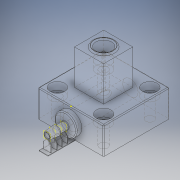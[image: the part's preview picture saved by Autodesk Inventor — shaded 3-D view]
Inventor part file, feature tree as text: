
AUTODESK INVENTOR PART (.ipt)
format: ipt  version: 2019 (Build 230136000, 136)  size: 399,360 bytes
history: native  units: mm
features: sketch x14, extrude x8, plane x7, projected_geometry x4, revolve x2, fillet x2, sweep x1, hole x1
ambient origin geometry x8: Origin, YZ Plane, XZ Plane, XY Plane, X Axis, Y Axis, Z Axis, Center Point
bodies: Solid1 (feature_tree)
feature tree (39):
  revolve  "Revolution1"  [1 undecoded]
  plane  "Work Plane1"
  extrude  "Extrusion1"  Depth=0.35mm
  plane  "Work Plane7"
  extrude  "Extrusion6"  Depth=0.75mm
  extrude  "Extrusion7"  TaperAngle=90.0deg  [1 undecoded]
  sketch  "Sketch17"  dims[d11=-0.75mm d12=0.75mm d13=2.0mm]
  plane  "Work Plane8"
  sweep  "Sweep3"
  fillet  "Fillet1"  Radius=2.0mm
  hole  "Hole3"  [1 undecoded]
  revolve  "Revolution2"  [1 undecoded]
  fillet  "Fillet2"  Radius=36.0mm
  plane  "Work Plane10"
  plane  "Work Plane11"
  plane  "Work Plane12"
  plane  "Work Plane13"
  extrude  "Extrusion8"  Depth=32.7mm TaperAngle=0.0deg
  extrude  "Extrusion9"  Depth=3.0mm
  extrude  "Extrusion10"  Depth=25.4mm
  extrude  "Extrusion11"  Depth=3.0mm
  extrude  "Extrusion12"  Depth=5.0mm
  sketch  "Sketch27"  dims[d83=0.25mm d84=2.413mm d85=5.08mm d86=1.15mm d87=0.25mm d88=0.25mm d89=90.0deg d90=0.5mm d92=0.0mm d93=-3.0mm d94=-6.0mm d95=-9.0mm d97=2.0mm d98=2.0mm d99=2.0mm d100=2.0mm d101=0.3mm d102=0.3mm d103=0.0mm d104=2.0mm d105=2.0mm d106=2.0mm d107=2.0mm d108=0.3mm d109=0.3mm d110=0.0mm d111=2.0mm d112=2.0mm d113=2.0mm d114=2.0mm d115=0.3mm d116=0.3mm d117=0.0mm d118=0.3mm d119=0.0mm d120=5.0mm d121=0.3mm d122=15.0mm d123=0.0mm]
  sketch  "Sketch1"  dims[d0=6.0mm d1=20.0mm]
  sketch  "Sketch2"  dims[d5=9.0mm d6=0.35mm]
  sketch  "Sketch11"  dims[d7=0.75mm d8=0.75mm]
  sketch  "Sketch16"  dims[d9=0.75mm d10=90.0deg]
  projected_geometry  "Projected Loop9"
  sketch  "Sketch18"  dims[d14=2.0mm d15=0.0mm d45=0.0mm]
  sketch  "Sketch19"  dims[d47=15.0mm d48=0.0mm d60=36.0mm d61=36.0mm]
  sketch  "Sketch21"  dims[d64=8.45mm d65=32.7mm d66=0.0mm]
  sketch  "Sketch22"  dims[d67=0.0mm d68=0.0mm d69=3.0mm]
  sketch  "Sketch23"  dims[d70=25.4mm d71=25.4mm]
  projected_geometry  "Projected Loop10"
  sketch  "Sketch24"  dims[d72=4.496mm d73=6.0mm d74=7.938mm d75=4.166mm d76=90.0deg d77=19.05mm d78=20.594885mm d79=3.0mm]
  projected_geometry  "Projected Loop11"
  sketch  "Sketch25"  dims[d80=6.0mm d81=5.0mm]
  projected_geometry  "Projected Loop12"
  sketch  "Sketch26"  dims[d82=1.8796mm]
note: 4 required parameter values undecoded (feature->parameter linkage not recoverable at this tier; creation-order binding heuristic only, values carry confidence <= 0.55)